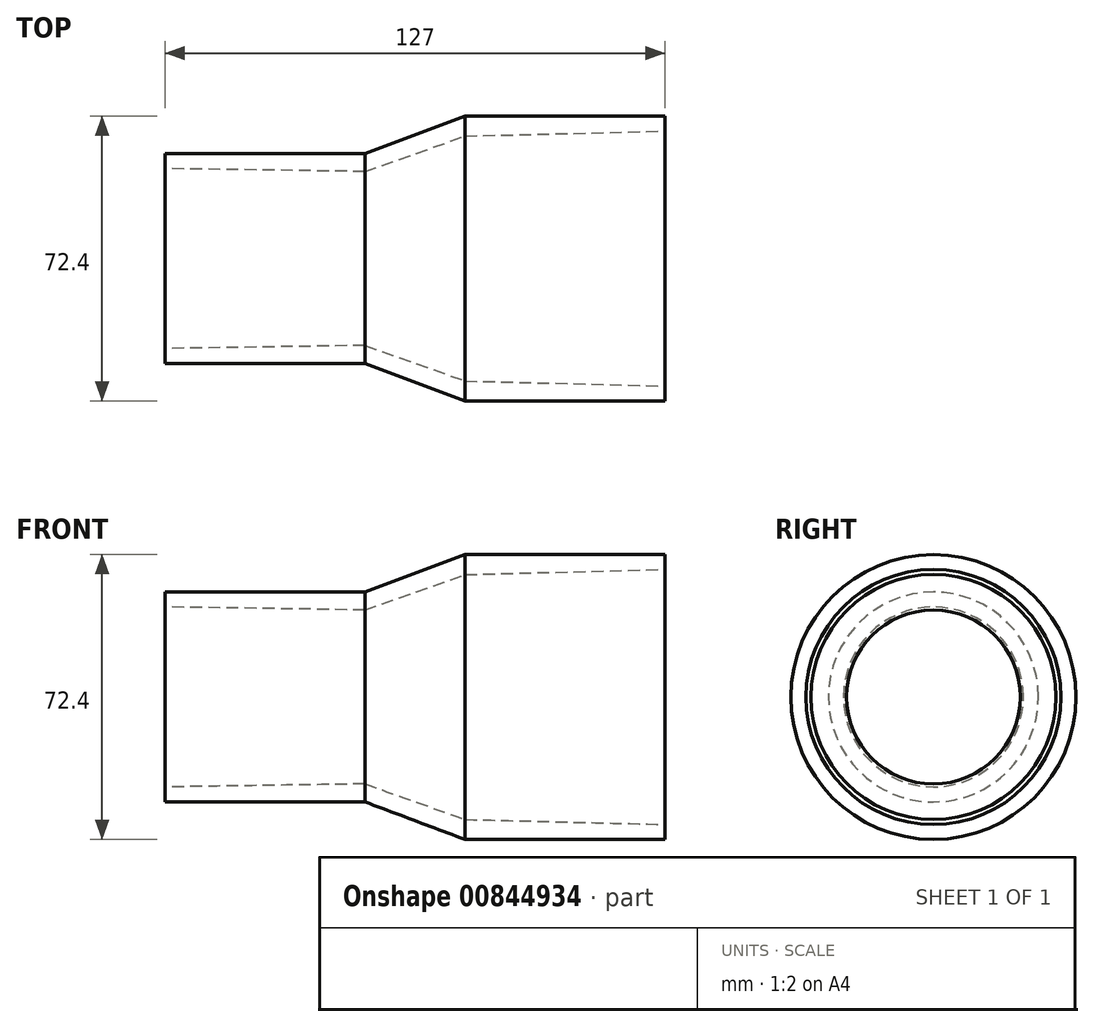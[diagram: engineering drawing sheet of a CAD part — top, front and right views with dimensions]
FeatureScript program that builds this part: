
annotation { "Feature Type Name" : "Feature", "Feature Type Description" : "" }
export const myFeature = defineFeature(function(context is Context, id is Id, definition is map)
    precondition{}
    {
        {
            var Q0;
            Q0=qCreatedBy(makeId("Front.planeOp"),FACE);
            var sketch = newSketch(context, id + "F0", { "sketchPlane" : qUnion([Q0])});
            skLineSegment(sketch, "E0", {"start": v(0, 0) * mm, "end": v(-90.9, 0) * mm, "construction": true});
            skLineSegment(sketch, "E1", {"start": v(0, 36.2) * mm, "end": v(50.8, 36.2) * mm});
            skLineSegment(sketch, "E2", {"start": v(50.8, 36.2) * mm, "end": v(50.8, 32.39) * mm});
            skLineSegment(sketch, "E3", {"start": v(50.8, 32.39) * mm, "end": v(0, 31.12) * mm});
            skLineSegment(sketch, "E4", {"start": v(0, 31.12) * mm, "end": v(-25.4, 22.1) * mm});
            skLineSegment(sketch, "E5", {"start": v(-25.4, 22.1) * mm, "end": v(-76.2, 22.86) * mm});
            skLineSegment(sketch, "E6", {"start": v(-76.2, 22.86) * mm, "end": v(-76.2, 26.67) * mm});
            skLineSegment(sketch, "E7", {"start": v(-76.2, 26.67) * mm, "end": v(-25.4, 26.67) * mm});
            skLineSegment(sketch, "E8", {"start": v(-25.4, 26.67) * mm, "end": v(0, 36.2) * mm});
            skPoint(sketch, "E9", {"position": v(25.4, 31.75) * mm});
            skPoint(sketch, "E10", {"position": v(-50.8, 22.48) * mm});
            skLineSegment(sketch, "E11", {"start": v(-25.4, 22.1) * mm, "end": v(-25.4, 26.67) * mm, "construction": true});
            skSolve(sketch);
        }
        {
            var Q0;
            Q0=qSketchRegion(id+"F0",true);
            var Q1;
            Q1=sQuery(id+"F0.wireOp",EDGE,"E0");
            revolve(context, id + "F1", {"surfaceOperationType" : NewSurfaceOperationType.NEW, "entities" : qUnion([Q0]), "axis" : qUnion([Q1]), "revolveType" : RevolveType.FULL});
        }
    });
